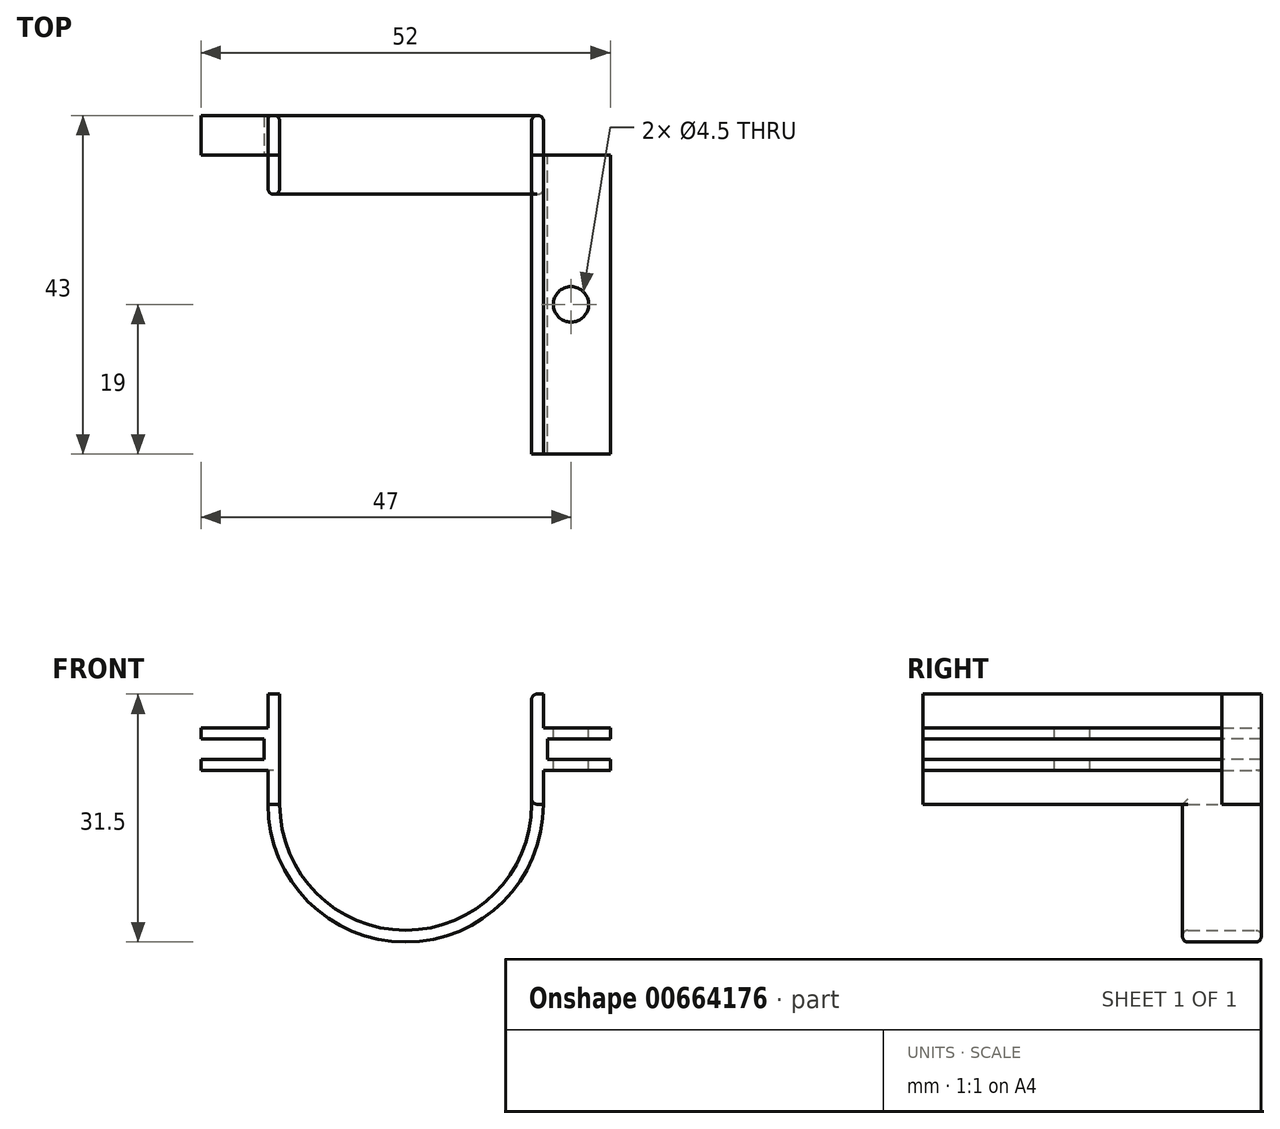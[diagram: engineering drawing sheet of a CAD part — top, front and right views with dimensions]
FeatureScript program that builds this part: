
annotation { "Feature Type Name" : "Feature", "Feature Type Description" : "" }
export const myFeature = defineFeature(function(context is Context, id is Id, definition is map)
    precondition{}
    {
        {
            var Q0;
            Q0=qCreatedBy(makeId("Front.planeOp"),FACE);
            var sketch = newSketch(context, id + "F0", { "sketchPlane" : qUnion([Q0])});
            skCircle(sketch, "E0", {"center": v(0, 0) * mm, "radius": 17.5 * mm});
            skLineSegment(sketch, "E1.bottom", {"start": v(-17.5, 0) * mm, "end": v(-17.5, 0) * mm});
            skLineSegment(sketch, "E1.left", {"start": v(-17.5, 0) * mm, "end": v(-17.5, 0) * mm});
            skLineSegment(sketch, "E2", {"start": v(-17.5, 0) * mm, "end": v(17.5, 0) * mm});
            skSolve(sketch);
        }
        {
            var Q0;
            {var subQ0=sQuery(id+"F0.wireOp",EDGE,"E2");Q0=makeQuery(id+"F0.imprint","IMPRINT",FACE,{"disambiguationData":[TD([[makeQuery(id+"F0.imprint","IMPRINT",EDGE,{"derivedFrom":subQ0}),-1.0]])]});}
            extrude(context, id + "F1", {"entities" : qUnion([Q0]), "endBound" : BoundingType.SYMMETRIC, "depth" : 10 * mm, "offsetDistance" : 25 * mm});
        }
        {
            var Q0;
            Q0=makeQuery(id+"F1.opExtrude","CAP_FACE",FACE,{"disambiguationData":[OSD([sQuery(id+"F0.wireOp",EDGE,"E0"),sQuery(id+"F0.wireOp",EDGE,"E1.top"),sQuery(id+"F0.wireOp",EDGE,"E1.left"),sQuery(id+"F0.wireOp",EDGE,"E1.right"),sQuery(id+"F0.wireOp",EDGE,"LefxOoeR-nq5w-59BA-Ikxv-zXAR8450YXsB.bottom"),sQuery(id+"F0.wireOp",EDGE,"LefxOoeR-nq5w-59BA-Ikxv-zXAR8450YXsB.top"),sQuery(id+"F0.wireOp",EDGE,"LefxOoeR-nq5w-59BA-Ikxv-zXAR8450YXsB.right"),sQuery(id+"F0.wireOp",EDGE,"BH197fx9-mUJi-XVLk-NfY7-dZP8ODIYXxIu.bottom"),sQuery(id+"F0.wireOp",EDGE,"BH197fx9-mUJi-XVLk-NfY7-dZP8ODIYXxIu.top"),sQuery(id+"F0.wireOp",EDGE,"BH197fx9-mUJi-XVLk-NfY7-dZP8ODIYXxIu.right")])],"isStart":false});
            var Q1;
            Q1=makeQuery(id+"F1.opExtrude","SWEPT_FACE",FACE,{"disambiguationData":[OSD([sQuery(id+"F0.wireOp",EDGE,"E1.top"),sQuery(id+"F0.wireOp",EDGE,"LefxOoeR-nq5w-59BA-Ikxv-zXAR8450YXsB.bottom"),sQuery(id+"F0.wireOp",EDGE,"BH197fx9-mUJi-XVLk-NfY7-dZP8ODIYXxIu.bottom")])]});
            var Q2;
            Q2=makeQuery(id+"F1.opExtrude","CAP_FACE",FACE,{"disambiguationData":[OSD([sQuery(id+"F0.wireOp",EDGE,"E0"),sQuery(id+"F0.wireOp",EDGE,"E1.top"),sQuery(id+"F0.wireOp",EDGE,"E1.left"),sQuery(id+"F0.wireOp",EDGE,"E1.right"),sQuery(id+"F0.wireOp",EDGE,"LefxOoeR-nq5w-59BA-Ikxv-zXAR8450YXsB.bottom"),sQuery(id+"F0.wireOp",EDGE,"LefxOoeR-nq5w-59BA-Ikxv-zXAR8450YXsB.top"),sQuery(id+"F0.wireOp",EDGE,"LefxOoeR-nq5w-59BA-Ikxv-zXAR8450YXsB.right"),sQuery(id+"F0.wireOp",EDGE,"BH197fx9-mUJi-XVLk-NfY7-dZP8ODIYXxIu.bottom"),sQuery(id+"F0.wireOp",EDGE,"BH197fx9-mUJi-XVLk-NfY7-dZP8ODIYXxIu.top"),sQuery(id+"F0.wireOp",EDGE,"BH197fx9-mUJi-XVLk-NfY7-dZP8ODIYXxIu.right")])],"isStart":true});
            var Q3;
            Q3=makeQuery(id+"F1.opExtrude","SWEPT_FACE",FACE,{"disambiguationData":[OSD([sQuery(id+"F0.wireOp",EDGE,"E2")])]});
            shell(context, id + "F2", {"entities" : qUnion([Q0, Q1, Q2, Q3]), "thickness" : 1.5 * mm});
        }
        {
            var Q0;
            Q0=qCreatedBy(makeId("Front.planeOp"),FACE);
            var sketch = newSketch(context, id + "F3", { "sketchPlane" : qUnion([Q0])});
            skLineSegment(sketch, "E3.bottom", {"start": v(-16, 0) * mm, "end": v(-26, 0) * mm});
            skLineSegment(sketch, "E3.top", {"start": v(-16, 14) * mm, "end": v(-26, 14) * mm});
            skLineSegment(sketch, "E3.left", {"start": v(-16, 0) * mm, "end": v(-16, 14) * mm});
            skLineSegment(sketch, "E3.right", {"start": v(-26, 0) * mm, "end": v(-26, 14) * mm});
            skLineSegment(sketch, "E4.bottom", {"start": v(-26, 8.3) * mm, "end": v(-18, 8.3) * mm});
            skLineSegment(sketch, "E4.top", {"start": v(-26, 5.7) * mm, "end": v(-18, 5.7) * mm});
            skLineSegment(sketch, "E4.left", {"start": v(-26, 8.3) * mm, "end": v(-26, 5.7) * mm});
            skLineSegment(sketch, "E4.right", {"start": v(-18, 8.3) * mm, "end": v(-18, 5.7) * mm});
            skLineSegment(sketch, "E5.MirrorCS", {"start": v(26, 8.3) * mm, "end": v(26, 5.7) * mm});
            skLineSegment(sketch, "E6.MirrorCS", {"start": v(26, 5.7) * mm, "end": v(18, 5.7) * mm});
            skLineSegment(sketch, "E7.MirrorCS", {"start": v(16, 0) * mm, "end": v(16, 14) * mm});
            skLineSegment(sketch, "E8.MirrorCS", {"start": v(16, 14) * mm, "end": v(26, 14) * mm});
            skLineSegment(sketch, "E9.MirrorCS", {"start": v(26, 8.3) * mm, "end": v(18, 8.3) * mm});
            skLineSegment(sketch, "E10.MirrorCS", {"start": v(16, 0) * mm, "end": v(26, 0) * mm});
            skLineSegment(sketch, "E11.MirrorCS", {"start": v(26, 0) * mm, "end": v(26, 14) * mm});
            skLineSegment(sketch, "E12.MirrorCS", {"start": v(18, 8.3) * mm, "end": v(18, 5.7) * mm});
            skSolve(sketch);
        }
        {
            var Q0;
            {var subQ2=sQuery(id+"F3.wireOp",EDGE,"E6.MirrorCS");Q0=makeQuery(id+"F3.imprint","IMPRINT",FACE,{"disambiguationData":[TD([[makeQuery(id+"F3.imprint","IMPRINT",EDGE,{"derivedFrom":subQ2}),1.0]])]});}
            extrude(context, id + "F4", {"entities" : qUnion([Q0]), "operationType" : NewBodyOperationType.ADD, "depth" : 38 * mm, "offsetDistance" : 25 * mm});
        }
        {
            var Q0;
            {var subQ1=sQuery(id+"F3.wireOp",EDGE,"E3.bottom");Q0=makeQuery(id+"F3.imprint","IMPRINT",FACE,{"disambiguationData":[TD([[makeQuery(id+"F3.imprint","IMPRINT",EDGE,{"derivedFrom":subQ1}),-1.0]])]});}
            extrude(context, id + "F5", {"entities" : qUnion([Q0]), "operationType" : NewBodyOperationType.ADD, "oppositeDirection" : true, "depth" : 5 * mm, "offsetDistance" : 25 * mm});
        }
        {
            var Q0;
            Q0=makeQuery(id+"F4.opExtrude","SWEPT_FACE",FACE,{"disambiguationData":[OSD([sQuery(id+"F3.wireOp",EDGE,"E8.MirrorCS")])]});
            var sketch = newSketch(context, id + "F6", { "sketchPlane" : qUnion([Q0])});
            skCircle(sketch, "E13", {"center": v(21, -19) * mm, "radius": 2.25 * mm});
            skSolve(sketch);
        }
        {
            var Q0;
            Q0=makeQuery(id+"F6.imprint","IMPRINT",FACE,{"disambiguationData":[TD([[makeQuery(id+"F6.imprint","IMPRINT",EDGE,{"derivedFrom":sQuery(id+"F6.wireOp",EDGE,"E13")}),1.0]])]});
            extrude(context, id + "F7", {"entities" : qUnion([Q0]), "operationType" : NewBodyOperationType.REMOVE, "endBound" : BoundingType.THROUGH_ALL, "oppositeDirection" : true, "depth" : 25 * mm, "offsetDistance" : 25 * mm});
        }
        {
            var Q0;
            Q0=makeQuery(id+"F5.boolean.opBoolean","MERGE",FACE,{"derivedFrom":[makeQuery(id+"F1.opExtrude","CAP_FACE",FACE,{"disambiguationData":[OSD([sQuery(id+"F0.wireOp",EDGE,"E0"),sQuery(id+"F0.wireOp",EDGE,"E2")])],"isStart":true}),makeQuery(id+"F5.opExtrude","CAP_FACE",FACE,{"disambiguationData":[OSD([sQuery(id+"F3.wireOp",EDGE,"E3.bottom"),sQuery(id+"F3.wireOp",EDGE,"E3.top"),sQuery(id+"F3.wireOp",EDGE,"E3.left"),sQuery(id+"F3.wireOp",EDGE,"E3.right"),sQuery(id+"F3.wireOp",EDGE,"E4.bottom"),sQuery(id+"F3.wireOp",EDGE,"E4.top"),sQuery(id+"F3.wireOp",EDGE,"E4.right")])],"isStart":false})]});
            var sketch = newSketch(context, id + "F8", { "sketchPlane" : qUnion([Q0])});
            skLineSegment(sketch, "E14.bottom", {"start": v(26, 0) * mm, "end": v(17.5, 0) * mm});
            skLineSegment(sketch, "E14.top", {"start": v(26, 4.3) * mm, "end": v(17.5, 4.3) * mm});
            skLineSegment(sketch, "E14.left", {"start": v(26, 0) * mm, "end": v(26, 4.3) * mm});
            skLineSegment(sketch, "E14.right", {"start": v(17.5, 0) * mm, "end": v(17.5, 4.3) * mm});
            skLineSegment(sketch, "E15.bottom", {"start": v(26, 14) * mm, "end": v(17.5, 14) * mm});
            skLineSegment(sketch, "E15.top", {"start": v(26, 9.7) * mm, "end": v(17.5, 9.7) * mm});
            skLineSegment(sketch, "E15.left", {"start": v(26, 14) * mm, "end": v(26, 9.7) * mm});
            skLineSegment(sketch, "E15.right", {"start": v(17.5, 14) * mm, "end": v(17.5, 9.7) * mm});
            skSolve(sketch);
        }
        {
            var Q0;
            Q0=makeQuery(id+"F8.imprint","IMPRINT",FACE,{"disambiguationData":[TD([[makeQuery(id+"F8.imprint","IMPRINT",EDGE,{"derivedFrom":sQuery(id+"F8.wireOp",EDGE,"E14.bottom")}),1.0]])]});
            var Q1;
            Q1=makeQuery(id+"F8.imprint","IMPRINT",FACE,{"disambiguationData":[TD([[makeQuery(id+"F8.imprint","IMPRINT",EDGE,{"derivedFrom":sQuery(id+"F8.wireOp",EDGE,"E15.bottom")}),-1.0]])]});
            extrude(context, id + "F9", {"entities" : qUnion([Q0, Q1]), "operationType" : NewBodyOperationType.REMOVE, "endBound" : BoundingType.THROUGH_ALL, "oppositeDirection" : true, "depth" : 25 * mm, "offsetDistance" : 25 * mm});
        }
        {
            var Q0;
            {var subQ2=sQuery(id+"F3.wireOp",EDGE,"E6.MirrorCS");Q0=makeQuery(id+"F3.imprint","IMPRINT",FACE,{"disambiguationData":[TD([[makeQuery(id+"F3.imprint","IMPRINT",EDGE,{"derivedFrom":subQ2}),1.0]])]});}
            var sketch = newSketch(context, id + "F10", { "sketchPlane" : qUnion([Q0])});
            skLineSegment(sketch, "E16.bottom", {"start": v(17.5, 0) * mm, "end": v(26, 0) * mm});
            skLineSegment(sketch, "E16.top", {"start": v(17.5, 4.3) * mm, "end": v(26, 4.3) * mm});
            skLineSegment(sketch, "E16.left", {"start": v(17.5, 0) * mm, "end": v(17.5, 4.3) * mm});
            skLineSegment(sketch, "E16.right", {"start": v(26, 0) * mm, "end": v(26, 4.3) * mm});
            skLineSegment(sketch, "E17.bottom", {"start": v(26, 14) * mm, "end": v(17.5, 14) * mm});
            skLineSegment(sketch, "E17.top", {"start": v(26, 9.7) * mm, "end": v(17.5, 9.7) * mm});
            skLineSegment(sketch, "E17.left", {"start": v(26, 14) * mm, "end": v(26, 9.7) * mm});
            skLineSegment(sketch, "E17.right", {"start": v(17.5, 14) * mm, "end": v(17.5, 9.7) * mm});
            skSolve(sketch);
        }
        {
            var Q0;
            Q0=makeQuery(id+"F10.imprint","IMPRINT",FACE,{"disambiguationData":[TD([[makeQuery(id+"F10.imprint","IMPRINT",EDGE,{"derivedFrom":sQuery(id+"F10.wireOp",EDGE,"E16.bottom")}),1.0]])]});
            var Q1;
            Q1=makeQuery(id+"F10.imprint","IMPRINT",FACE,{"disambiguationData":[TD([[makeQuery(id+"F10.imprint","IMPRINT",EDGE,{"derivedFrom":sQuery(id+"F10.wireOp",EDGE,"E17.bottom")}),-1.0]])]});
            extrude(context, id + "F11", {"entities" : qUnion([Q0, Q1]), "operationType" : NewBodyOperationType.REMOVE, "endBound" : BoundingType.THROUGH_ALL, "depth" : 25 * mm, "offsetDistance" : 25 * mm});
        }
        {
            var Q0;
            {var subQ0=sQuery(id+"F0.wireOp",EDGE,"E0");Q0=makeQuery(id+"F2.opShell","OFFSET_EDGE",EDGE,{"disambiguationData":[OSD([subQ0]),TDD([makeQuery(id+"F1.opExtrude","CAP_EDGE",EDGE,{"disambiguationData":[OSD([subQ0])],"isStart":false})])]});}
            var Q1;
            {var subQ0=sQuery(id+"F0.wireOp",EDGE,"E0");Q1=makeQuery(id+"F2.opShell","OFFSET_EDGE",EDGE,{"disambiguationData":[OSD([subQ0]),TDD([makeQuery(id+"F1.opExtrude","CAP_EDGE",EDGE,{"disambiguationData":[OSD([subQ0])],"isStart":true})])]});}
            var Q2;
            Q2=makeQuery(id+"F11.boolean.opBoolean","COPY",EDGE,{"derivedFrom":makeQuery(id+"F11.opExtrude","SWEPT_EDGE",EDGE,{"disambiguationData":[OSD([sQuery(id+"F3.wireOp",EDGE,"E11.MirrorCS"),sQuery(id+"F10.wireOp",EDGE,"E16.top"),sQuery(id+"F10.wireOp",EDGE,"E16.right")])]})});
            var Q3;
            Q3=makeQuery(id+"F11.boolean.opBoolean","COPY",EDGE,{"derivedFrom":makeQuery(id+"F11.opExtrude","SWEPT_EDGE",EDGE,{"disambiguationData":[OSD([sQuery(id+"F3.wireOp",EDGE,"E10.MirrorCS"),sQuery(id+"F10.wireOp",EDGE,"E16.bottom"),sQuery(id+"F10.wireOp",EDGE,"E16.left")])]})});
            var Q4;
            Q4=makeQuery(id+"F1.opExtrude","CAP_EDGE",EDGE,{"disambiguationData":[OSD([sQuery(id+"F0.wireOp",EDGE,"E0")])],"isStart":false});
            var Q5;
            Q5=makeQuery(id+"F9.boolean.opBoolean","COPY",EDGE,{"derivedFrom":makeQuery(id+"F9.opExtrude","SWEPT_EDGE",EDGE,{"disambiguationData":[OSD([sQuery(id+"F3.wireOp",EDGE,"E3.right"),sQuery(id+"F8.wireOp",EDGE,"E14.top"),sQuery(id+"F8.wireOp",EDGE,"E14.left")])]})});
            var Q6;
            Q6=makeQuery(id+"F1.opExtrude","CAP_EDGE",EDGE,{"disambiguationData":[OSD([sQuery(id+"F0.wireOp",EDGE,"E0")])],"isStart":true});
            var Q7;
            Q7=makeQuery(id+"F11.boolean.opBoolean","COPY",EDGE,{"derivedFrom":makeQuery(id+"F11.opExtrude","SWEPT_EDGE",EDGE,{"disambiguationData":[OSD([sQuery(id+"F3.wireOp",EDGE,"E8.MirrorCS"),sQuery(id+"F10.wireOp",EDGE,"E17.bottom"),sQuery(id+"F10.wireOp",EDGE,"E17.right")])]})});
            var Q8;
            Q8=makeQuery(id+"F9.boolean.opBoolean","COPY",EDGE,{"derivedFrom":makeQuery(id+"F9.opExtrude","SWEPT_EDGE",EDGE,{"disambiguationData":[OSD([sQuery(id+"F3.wireOp",EDGE,"E3.right"),sQuery(id+"F8.wireOp",EDGE,"E15.top"),sQuery(id+"F8.wireOp",EDGE,"E15.left")])]})});
            var Q9;
            Q9=makeQuery(id+"F11.boolean.opBoolean","COPY",EDGE,{"derivedFrom":makeQuery(id+"F11.opExtrude","SWEPT_EDGE",EDGE,{"disambiguationData":[OSD([sQuery(id+"F3.wireOp",EDGE,"E11.MirrorCS"),sQuery(id+"F10.wireOp",EDGE,"E17.top"),sQuery(id+"F10.wireOp",EDGE,"E17.left")])]})});
            var Q10;
            Q10=makeQuery(id+"F4.opExtrude","SWEPT_EDGE",EDGE,{"disambiguationData":[OSD([sQuery(id+"F3.wireOp",EDGE,"E7.MirrorCS"),sQuery(id+"F3.wireOp",EDGE,"E8.MirrorCS")])]});
            var Q11;
            Q11=makeQuery(id+"F4.boolean.opBoolean","SPLIT",EDGE,{"derivedFrom":makeQuery(id+"F4.opExtrude","SWEPT_EDGE",EDGE,{"disambiguationData":[OSD([sQuery(id+"F3.wireOp",EDGE,"E7.MirrorCS"),sQuery(id+"F3.wireOp",EDGE,"E10.MirrorCS")])]})});
            fillet(context, id + "F12", {"entities" : qUnion([Q0, Q1, Q2, Q3, Q4, Q5, Q6, Q7, Q8, Q9, Q10, Q11]), "radius" : 0.7 * mm, "tangentPropagation" : true, "allowEdgeOverflow" : false});
        }
    });
